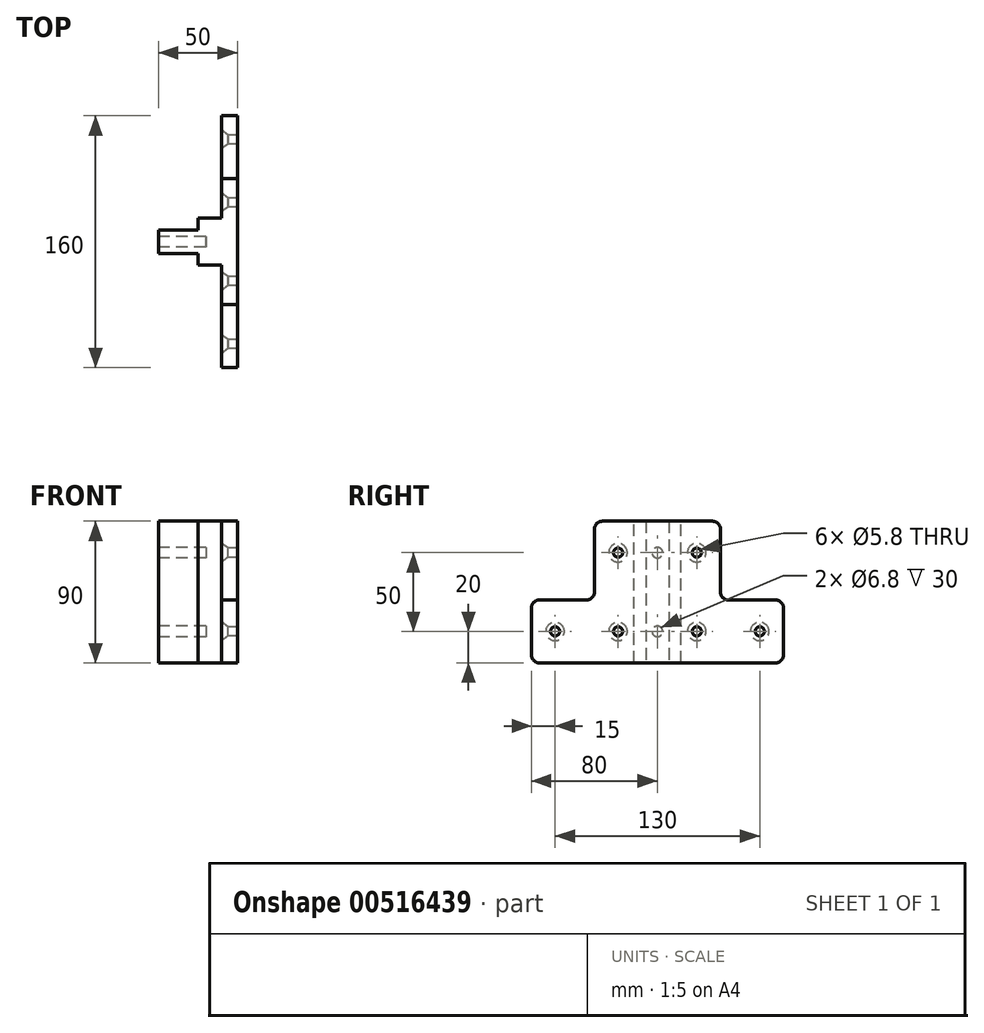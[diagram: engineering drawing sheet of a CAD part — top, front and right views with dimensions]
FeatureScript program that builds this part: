
annotation { "Feature Type Name" : "Feature", "Feature Type Description" : "" }
export const myFeature = defineFeature(function(context is Context, id is Id, definition is map)
    precondition{}
    {
        {
            var Q0;
            Q0=qCreatedBy(makeId("Right.planeOp"),FACE);
            var sketch = newSketch(context, id + "F0", { "sketchPlane" : qUnion([Q0])});
            skLineSegment(sketch, "E0.bottom", {"start": v(75, -45) * mm, "end": v(-75, -45) * mm});
            skLineSegment(sketch, "E0.top", {"start": v(35, 45) * mm, "end": v(-35, 45) * mm});
            skLineSegment(sketch, "E0.left", {"start": v(80, -40) * mm, "end": v(80, -10) * mm});
            skLineSegment(sketch, "E0.right", {"start": v(-80, -40) * mm, "end": v(-80, -10) * mm});
            skPoint(sketch, "E0.middle", {"position": v(0, 0) * mm});
            skLineSegment(sketch, "E1.top", {"start": v(-75, -5) * mm, "end": v(-45, -5) * mm});
            skLineSegment(sketch, "E1.right", {"start": v(-40, 40) * mm, "end": v(-40, 0) * mm});
            skLineSegment(sketch, "E2.top", {"start": v(75, -5) * mm, "end": v(45, -5) * mm});
            skLineSegment(sketch, "E2.right", {"start": v(40, 40) * mm, "end": v(40, 0) * mm});
            skPoint(sketch, "E3.orphan", {"position": v(-80, 45) * mm});
            skPoint(sketch, "E4.orphan", {"position": v(80, 45) * mm});
            skPoint(sketch, "E5.visualSharp", {"position": v(-40, -5) * mm});
            skArc(sketch, "E5.filletArc", {"start": v(-45, -5) * mm, "mid": v(-41.46, -3.54) * mm, "end": v(-40, 0) * mm});
            skPoint(sketch, "E6.visualSharp", {"position": v(40, -5) * mm});
            skArc(sketch, "E6.filletArc", {"start": v(40, 0) * mm, "mid": v(41.46, -3.54) * mm, "end": v(45, -5) * mm});
            skPoint(sketch, "E7.visualSharp", {"position": v(80, -5) * mm});
            skArc(sketch, "E7.filletArc", {"start": v(80, -10) * mm, "mid": v(78.54, -6.46) * mm, "end": v(75, -5) * mm});
            skPoint(sketch, "E8.visualSharp", {"position": v(80, -45) * mm});
            skArc(sketch, "E8.filletArc", {"start": v(75, -45) * mm, "mid": v(78.54, -43.54) * mm, "end": v(80, -40) * mm});
            skPoint(sketch, "E9.visualSharp", {"position": v(-80, -45) * mm});
            skArc(sketch, "E9.filletArc", {"start": v(-80, -40) * mm, "mid": v(-78.54, -43.54) * mm, "end": v(-75, -45) * mm});
            skPoint(sketch, "E10.visualSharp", {"position": v(-80, -5) * mm});
            skArc(sketch, "E10.filletArc", {"start": v(-75, -5) * mm, "mid": v(-78.54, -6.46) * mm, "end": v(-80, -10) * mm});
            skPoint(sketch, "E11.visualSharp", {"position": v(-40, 45) * mm});
            skArc(sketch, "E11.filletArc", {"start": v(-35, 45) * mm, "mid": v(-38.54, 43.54) * mm, "end": v(-40, 40) * mm});
            skPoint(sketch, "E12.visualSharp", {"position": v(40, 45) * mm});
            skArc(sketch, "E12.filletArc", {"start": v(40, 40) * mm, "mid": v(38.54, 43.54) * mm, "end": v(35, 45) * mm});
            skCircle(sketch, "E13", {"center": v(-25, 25) * mm, "radius": 2.9 * mm});
            skCircle(sketch, "E14.0.1.0", {"center": v(-25, -25) * mm, "radius": 2.9 * mm});
            skCircle(sketch, "E14.1.0.0", {"center": v(25, 25) * mm, "radius": 2.9 * mm});
            skCircle(sketch, "E14.1.1.0", {"center": v(25, -25) * mm, "radius": 2.9 * mm});
            skLineSegment(sketch, "E14.direction1", {"start": v(-25, 25) * mm, "end": v(25, 25) * mm, "construction": true});
            skLineSegment(sketch, "E14.direction2", {"start": v(-25, 25) * mm, "end": v(-25, -25) * mm, "construction": true});
            skCircle(sketch, "E15.1.0.0", {"center": v(-65, -25) * mm, "radius": 2.9 * mm});
            skLineSegment(sketch, "E15.direction1", {"start": v(-25, -25) * mm, "end": v(-65, -25) * mm, "construction": true});
            skCircle(sketch, "E16.1.0.0", {"center": v(65, -25) * mm, "radius": 2.9 * mm});
            skLineSegment(sketch, "E16.direction1", {"start": v(25, -25) * mm, "end": v(65, -25) * mm, "construction": true});
            skSolve(sketch);
        }
        {
            var Q0;
            Q0 = qSketchRegion(id + "F0", true);
            extrude(context, id + "F1", {"entities" : qUnion([Q0]), "depth" : 10 * mm, "offsetDistance" : 25 * mm});
        }
        {
            var Q0;
            Q0=makeQuery(id+"F1.opExtrude","CAP_FACE",FACE,{"disambiguationData":[OSD([sQuery(id+"F0.wireOp",EDGE,"E0.bottom"),sQuery(id+"F0.wireOp",EDGE,"E0.top"),sQuery(id+"F0.wireOp",EDGE,"E0.left"),sQuery(id+"F0.wireOp",EDGE,"E0.right"),sQuery(id+"F0.wireOp",EDGE,"E1.top"),sQuery(id+"F0.wireOp",EDGE,"E1.right"),sQuery(id+"F0.wireOp",EDGE,"E2.top"),sQuery(id+"F0.wireOp",EDGE,"E2.right"),sQuery(id+"F0.wireOp",EDGE,"E5.filletArc"),sQuery(id+"F0.wireOp",EDGE,"E6.filletArc"),sQuery(id+"F0.wireOp",EDGE,"E7.filletArc"),sQuery(id+"F0.wireOp",EDGE,"E8.filletArc"),sQuery(id+"F0.wireOp",EDGE,"E9.filletArc"),sQuery(id+"F0.wireOp",EDGE,"E10.filletArc"),sQuery(id+"F0.wireOp",EDGE,"E11.filletArc"),sQuery(id+"F0.wireOp",EDGE,"E12.filletArc"),sQuery(id+"F0.wireOp",EDGE,"E13"),sQuery(id+"F0.wireOp",EDGE,"E14.0.1.0"),sQuery(id+"F0.wireOp",EDGE,"E14.1.0.0"),sQuery(id+"F0.wireOp",EDGE,"E14.1.1.0"),sQuery(id+"F0.wireOp",EDGE,"E15.1.0.0"),sQuery(id+"F0.wireOp",EDGE,"E16.1.0.0")])],"isStart":true});
            var sketch = newSketch(context, id + "F2", { "sketchPlane" : qUnion([Q0])});
            skLineSegment(sketch, "E17.bottom", {"start": v(-14.95, -45) * mm, "end": v(14.95, -45) * mm});
            skLineSegment(sketch, "E17.top", {"start": v(-14.95, 45) * mm, "end": v(14.95, 45) * mm});
            skLineSegment(sketch, "E17.left", {"start": v(-14.95, -45) * mm, "end": v(-14.95, 45) * mm});
            skLineSegment(sketch, "E17.right", {"start": v(14.95, -45) * mm, "end": v(14.95, 45) * mm});
            skPoint(sketch, "E17.middle", {"position": v(0, 0) * mm});
            skSolve(sketch);
        }
        {
            var Q0;
            Q0 = qSketchRegion(id + "F2", true);
            extrude(context, id + "F3", {"entities" : qUnion([Q0]), "operationType" : NewBodyOperationType.ADD, "depth" : 40 * mm, "offsetDistance" : 25 * mm});
        }
        {
            var Q0;
            Q0=makeQuery(id+"F3.opExtrude","CAP_FACE",FACE,{"disambiguationData":[OSD([sQuery(id+"F2.wireOp",EDGE,"E17.bottom"),sQuery(id+"F2.wireOp",EDGE,"E17.top"),sQuery(id+"F2.wireOp",EDGE,"E17.left"),sQuery(id+"F2.wireOp",EDGE,"E17.right")])],"isStart":false});
            var sketch = newSketch(context, id + "F4", { "sketchPlane" : qUnion([Q0])});
            skLineSegment(sketch, "E18.bottom", {"start": v(-14.95, 45) * mm, "end": v(-7.35, 45) * mm});
            skLineSegment(sketch, "E18.top", {"start": v(-14.95, -45) * mm, "end": v(-7.35, -45) * mm});
            skLineSegment(sketch, "E18.left", {"start": v(-14.95, 45) * mm, "end": v(-14.95, -45) * mm});
            skLineSegment(sketch, "E18.right", {"start": v(-7.35, 45) * mm, "end": v(-7.35, -45) * mm});
            skLineSegment(sketch, "E19.bottom", {"start": v(14.95, 45) * mm, "end": v(7.35, 45) * mm});
            skLineSegment(sketch, "E19.top", {"start": v(14.95, -45) * mm, "end": v(7.35, -45) * mm});
            skLineSegment(sketch, "E19.left", {"start": v(14.95, 45) * mm, "end": v(14.95, -45) * mm});
            skLineSegment(sketch, "E19.right", {"start": v(7.35, 45) * mm, "end": v(7.35, -45) * mm});
            skSolve(sketch);
        }
        {
            var Q0;
            Q0 = qSketchRegion(id + "F4", true);
            extrude(context, id + "F5", {"entities" : qUnion([Q0]), "operationType" : NewBodyOperationType.REMOVE, "oppositeDirection" : true, "depth" : 25 * mm, "offsetDistance" : 25 * mm});
        }
        {
            var Q0;
            Q0=makeQuery(id+"F3.opExtrude","CAP_FACE",FACE,{"disambiguationData":[OSD([sQuery(id+"F2.wireOp",EDGE,"E17.bottom"),sQuery(id+"F2.wireOp",EDGE,"E17.top"),sQuery(id+"F2.wireOp",EDGE,"E17.left"),sQuery(id+"F2.wireOp",EDGE,"E17.right")])],"isStart":false});
            var sketch = newSketch(context, id + "F6", { "sketchPlane" : qUnion([Q0])});
            skCircle(sketch, "E20", {"center": v(0, 25) * mm, "radius": 3.4 * mm});
            skPoint(sketch, "E20.centerSnap0", {"position": v(0, 45) * mm});
            skCircle(sketch, "E21", {"center": v(0, -25) * mm, "radius": 3.4 * mm});
            skSolve(sketch);
        }
        {
            var Q0;
            Q0 = qSketchRegion(id + "F6", true);
            extrude(context, id + "F7", {"entities" : qUnion([Q0]), "operationType" : NewBodyOperationType.REMOVE, "oppositeDirection" : true, "depth" : 30 * mm, "offsetDistance" : 25 * mm});
        }
        {
            var Q0;
            Q0=makeQuery(id+"F1.opExtrude","CAP_EDGE",EDGE,{"disambiguationData":[OSD([sQuery(id+"F0.wireOp",EDGE,"E14.1.0.0")])],"isStart":true});
            var Q1;
            Q1=makeQuery(id+"F1.opExtrude","CAP_EDGE",EDGE,{"disambiguationData":[OSD([sQuery(id+"F0.wireOp",EDGE,"E13")])],"isStart":true});
            var Q2;
            Q2=makeQuery(id+"F1.opExtrude","CAP_EDGE",EDGE,{"disambiguationData":[OSD([sQuery(id+"F0.wireOp",EDGE,"E15.1.0.0")])],"isStart":true});
            var Q3;
            Q3=makeQuery(id+"F1.opExtrude","CAP_EDGE",EDGE,{"disambiguationData":[OSD([sQuery(id+"F0.wireOp",EDGE,"E14.0.1.0")])],"isStart":true});
            var Q4;
            Q4=makeQuery(id+"F1.opExtrude","CAP_EDGE",EDGE,{"disambiguationData":[OSD([sQuery(id+"F0.wireOp",EDGE,"E14.1.1.0")])],"isStart":true});
            var Q5;
            Q5=makeQuery(id+"F1.opExtrude","CAP_EDGE",EDGE,{"disambiguationData":[OSD([sQuery(id+"F0.wireOp",EDGE,"E16.1.0.0")])],"isStart":true});
            chamfer(context, id + "F8", {"entities" : qUnion([Q0, Q1, Q2, Q3, Q4, Q5]), "chamferType" : ChamferType.TWO_OFFSETS, "width1" : 3 * mm, "oppositeDirection" : false, "width2" : 4 * mm, "tangentPropagation" : true});
        }
    });
